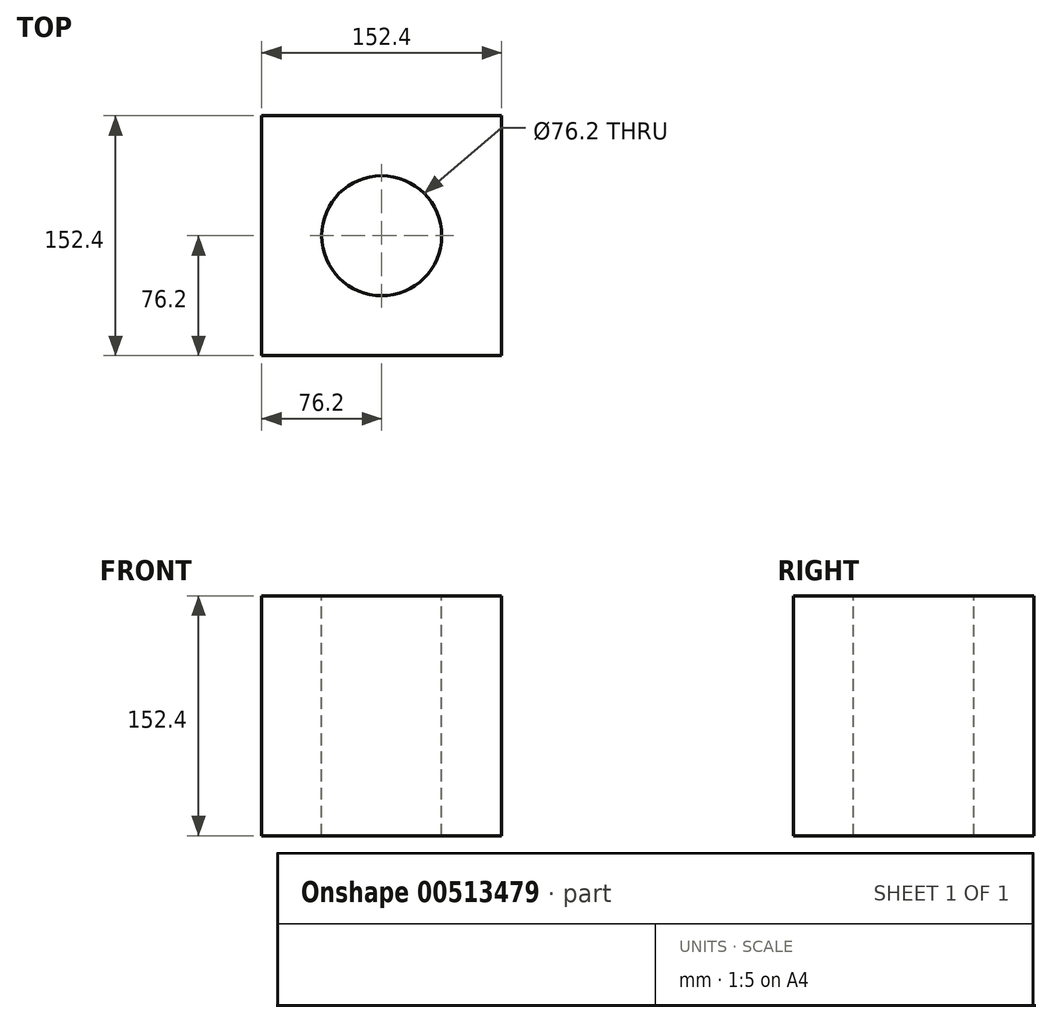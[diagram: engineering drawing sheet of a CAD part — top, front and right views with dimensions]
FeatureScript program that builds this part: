
annotation { "Feature Type Name" : "Feature", "Feature Type Description" : "" }
export const myFeature = defineFeature(function(context is Context, id is Id, definition is map)
    precondition{}
    {
        {
            var Q0;
            Q0=qCreatedBy(makeId("Top.planeOp"),FACE);
            var sketch = newSketch(context, id + "F0", { "sketchPlane" : qUnion([Q0])});
            skLineSegment(sketch, "E0.bottom", {"start": v(-76.2, 76.2) * mm, "end": v(76.2, 76.2) * mm});
            skLineSegment(sketch, "E0.top", {"start": v(-76.2, -76.2) * mm, "end": v(76.2, -76.2) * mm});
            skLineSegment(sketch, "E0.left", {"start": v(-76.2, 76.2) * mm, "end": v(-76.2, -76.2) * mm});
            skLineSegment(sketch, "E0.right", {"start": v(76.2, 76.2) * mm, "end": v(76.2, -76.2) * mm});
            skPoint(sketch, "E0.middle", {"position": v(0, 0) * mm});
            skSolve(sketch);
        }
        {
            var Q0;
            Q0 = qSketchRegion(id + "F0", true);
            extrude(context, id + "F1", {"entities" : qUnion([Q0]), "depth" : 152.4 * mm});
        }
        {
            var Q0;
            Q0=makeQuery(id+"F1.opExtrude","CAP_FACE",FACE,{"disambiguationData":[OSD([sQuery(id+"F0.wireOp",EDGE,"E0.bottom"),sQuery(id+"F0.wireOp",EDGE,"E0.top"),sQuery(id+"F0.wireOp",EDGE,"E0.left"),sQuery(id+"F0.wireOp",EDGE,"E0.right")])],"isStart":false});
            var sketch = newSketch(context, id + "F2", { "sketchPlane" : qUnion([Q0])});
            skCircle(sketch, "E1", {"center": v(0, 0) * mm, "radius": 38.1 * mm});
            skSolve(sketch);
        }
        {
            var Q0;
            Q0=makeQuery(id+"F2.imprint","IMPRINT",FACE,{"disambiguationData":[TD([[makeQuery(id+"F2.imprint","IMPRINT",EDGE,{"derivedFrom":sQuery(id+"F2.wireOp",EDGE,"E1")}),1.0]])]});
            extrude(context, id + "F3", {"entities" : qUnion([Q0]), "operationType" : NewBodyOperationType.REMOVE, "oppositeDirection" : true, "depth" : 152.4 * mm});
        }
    });
